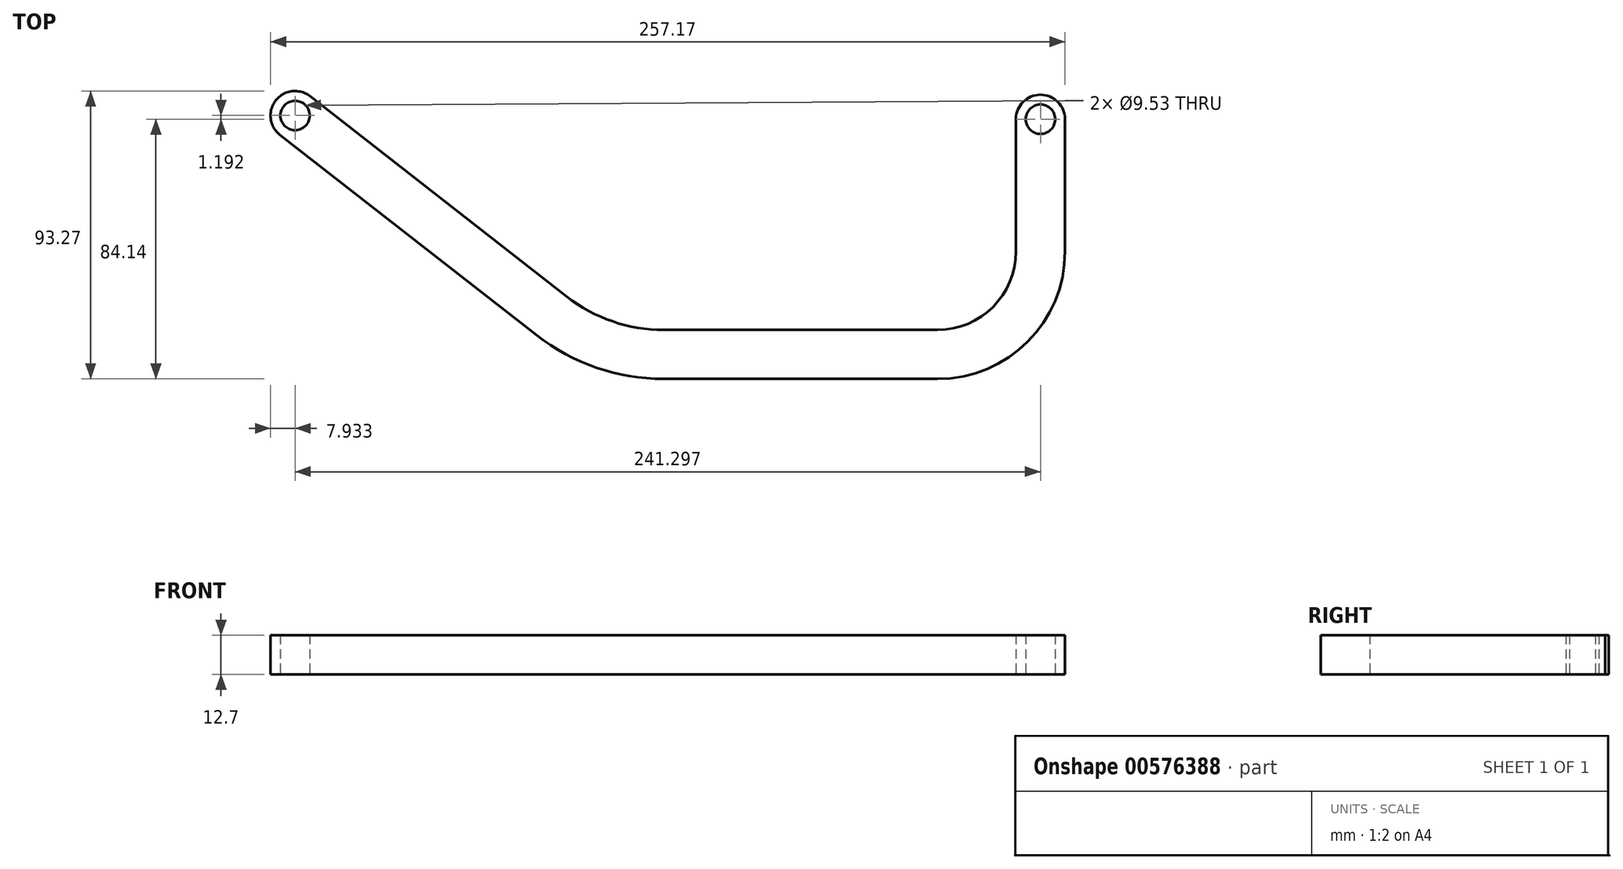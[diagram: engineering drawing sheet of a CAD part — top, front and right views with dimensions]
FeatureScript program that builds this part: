
annotation { "Feature Type Name" : "Feature", "Feature Type Description" : "" }
export const myFeature = defineFeature(function(context is Context, id is Id, definition is map)
    precondition{}
    {
        {
            var Q0;
            Q0=qCreatedBy(makeId("Top.planeOp"),FACE);
            var sketch = newSketch(context, id + "F0", { "sketchPlane" : qUnion([Q0])});
            skLineSegment(sketch, "E0", {"start": v(0, 0) * mm, "end": v(0, -76.2) * mm});
            skLineSegment(sketch, "E1", {"start": v(0, -76.2) * mm, "end": v(-142.24, -76.2) * mm});
            skLineSegment(sketch, "E2", {"start": v(-142.24, -76.2) * mm, "end": v(-241.3, 1.2) * mm});
            skSolve(sketch);
        }
        {
            var Q0;
            Q0=qCreatedBy(makeId("Top.planeOp"),FACE);
            var sketch = newSketch(context, id + "F1", { "sketchPlane" : qUnion([Q0])});
            skLineSegment(sketch, "E3.0", {"start": v(-153.3, -57.5) * mm, "end": v(-236.41, 7.45) * mm});
            skLineSegment(sketch, "E3.1", {"start": v(-33.34, -68.26) * mm, "end": v(-122.02, -68.26) * mm});
            skLineSegment(sketch, "E3.2", {"start": v(-7.94, 0) * mm, "end": v(-7.94, -42.86) * mm});
            skLineSegment(sketch, "E4.0", {"start": v(-163.06, -70) * mm, "end": v(-246.18, -5.06) * mm});
            skLineSegment(sketch, "E4.1", {"start": v(-33.34, -84.14) * mm, "end": v(-122.02, -84.14) * mm});
            skLineSegment(sketch, "E4.2", {"start": v(7.94, 0) * mm, "end": v(7.94, -42.86) * mm});
            skPoint(sketch, "E5.0", {"position": v(-241.3, 1.2) * mm});
            skPoint(sketch, "E6.0", {"position": v(0, 0) * mm});
            skCircle(sketch, "E7", {"center": v(-241.3, 1.2) * mm, "radius": 7.94 * mm});
            skCircle(sketch, "E8", {"center": v(0, 0) * mm, "radius": 7.94 * mm});
            skPoint(sketch, "E9.visualSharp", {"position": v(-139.5, -68.26) * mm});
            skArc(sketch, "E9.filletArc", {"start": v(-153.3, -57.5) * mm, "mid": v(-138.55, -65.5) * mm, "end": v(-122.02, -68.26) * mm});
            skPoint(sketch, "E10.visualSharp", {"position": v(-144.97, -84.14) * mm});
            skArc(sketch, "E10.filletArc", {"start": v(-163.06, -70) * mm, "mid": v(-143.72, -80.5) * mm, "end": v(-122.02, -84.14) * mm});
            skPoint(sketch, "E11.visualSharp", {"position": v(-7.94, -68.26) * mm});
            skArc(sketch, "E11.filletArc", {"start": v(-33.34, -68.26) * mm, "mid": v(-15.38, -60.82) * mm, "end": v(-7.94, -42.86) * mm});
            skPoint(sketch, "E12.visualSharp", {"position": v(7.94, -84.14) * mm});
            skArc(sketch, "E12.filletArc", {"start": v(-33.34, -84.14) * mm, "mid": v(-4.15, -72.05) * mm, "end": v(7.94, -42.86) * mm});
            skSolve(sketch);
        }
        {
            var Q0;
            {var subQ4=sQuery(id+"F1.wireOp",EDGE,"E3.0");Q0=makeQuery(id+"F1.imprint","IMPRINT",FACE,{"disambiguationData":[TD([[makeQuery(id+"F1.imprint","IMPRINT",EDGE,{"derivedFrom":subQ4}),1.0]])]});}
            var Q1;
            {var subQ0=sQuery(id+"F1.wireOp",EDGE,"E7");var subQ1=makeQuery(id+"F1.imprint","INTERSECT",VERTEX,{"derivedFrom":[sQuery(id+"F1.wireOp",EDGE,"E3.0"),subQ0]});Q1=makeQuery(id+"F1.imprint","IMPRINT",FACE,{"disambiguationData":[TD([[makeQuery(id+"F1.imprint","IMPRINT",EDGE,{"disambiguationData":[TD([[subQ1,-1.0]])],"derivedFrom":subQ0}),1.0]])]});}
            var Q2;
            {var subQ0=sQuery(id+"F1.wireOp",EDGE,"E8");var subQ1=makeQuery(id+"F1.imprint","INTERSECT",VERTEX,{"derivedFrom":[sQuery(id+"F1.wireOp",EDGE,"E3.2"),subQ0]});Q2=makeQuery(id+"F1.imprint","IMPRINT",FACE,{"disambiguationData":[TD([[makeQuery(id+"F1.imprint","IMPRINT",EDGE,{"disambiguationData":[TD([[subQ1,1.0]])],"derivedFrom":subQ0}),1.0]])]});}
            extrude(context, id + "F2", {"entities" : qUnion([Q0, Q1, Q2]), "depth" : 12.7 * mm, "offsetDistance" : 25.4 * mm});
        }
        {
            var Q0;
            Q0=sQuery(id+"F0.wireOp",VERTEX,"E2.end");
            var Q1;
            Q1=sQuery(id+"F0.wireOp",VERTEX,"E0.start");
            var Q2;
            Q2=makeQuery(id+"F2.opExtrude","SWEPT_BODY",BODY,{"disambiguationData":[OSD([sQuery(id+"F1.wireOp",EDGE,"E3.0"),sQuery(id+"F1.wireOp",EDGE,"E3.1"),sQuery(id+"F1.wireOp",EDGE,"E3.2"),sQuery(id+"F1.wireOp",EDGE,"E4.0"),sQuery(id+"F1.wireOp",EDGE,"E4.1"),sQuery(id+"F1.wireOp",EDGE,"E4.2"),sQuery(id+"F1.wireOp",EDGE,"E7"),sQuery(id+"F1.wireOp",EDGE,"E8"),sQuery(id+"F1.wireOp",EDGE,"E9.filletArc"),sQuery(id+"F1.wireOp",EDGE,"E10.filletArc"),sQuery(id+"F1.wireOp",EDGE,"E11.filletArc"),sQuery(id+"F1.wireOp",EDGE,"E12.filletArc")])]});
            hole(context, id + "F3", {"style" : HoleStyle.SIMPLE, "endStyle" : HoleEndStyle.THROUGH, "oppositeDirection" : true, "holeDiameter" : 9.52 * mm, "isTappedThrough" : true, "tappedDepth" : 12.7 * mm, "tapClearance" : 3, "locations" : qUnion([Q0, Q1]), "scope" : qUnion([Q2])});
        }
    });
